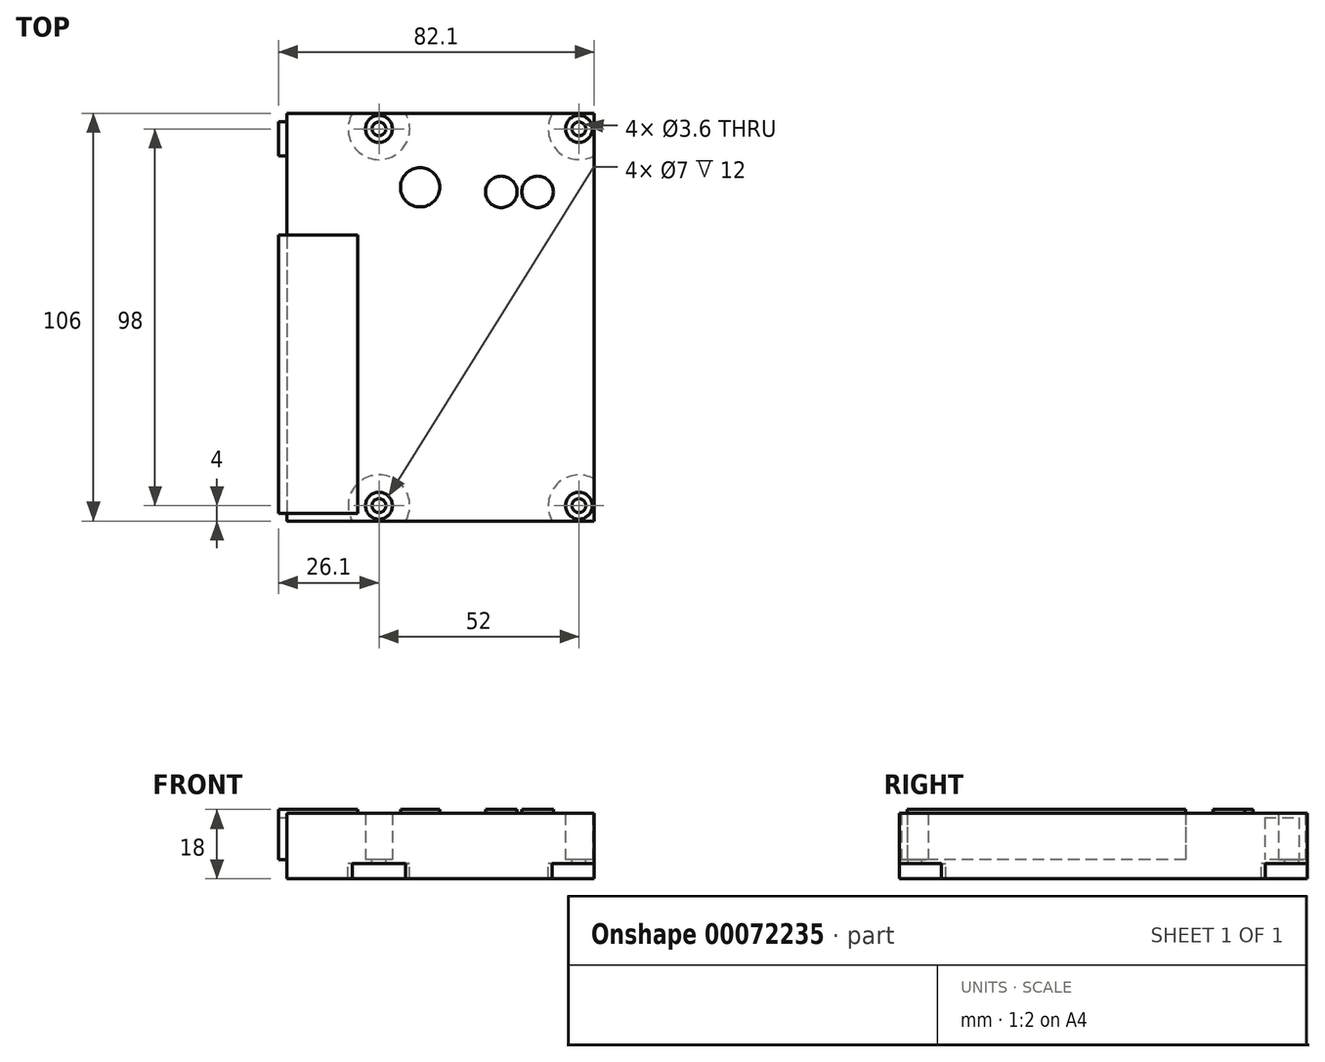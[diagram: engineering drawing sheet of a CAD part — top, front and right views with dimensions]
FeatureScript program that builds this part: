
annotation { "Feature Type Name" : "Feature", "Feature Type Description" : "" }
export const myFeature = defineFeature(function(context is Context, id is Id, definition is map)
    precondition{}
    {
        {
            var Q0;
            Q0=qCreatedBy(makeId("Top.planeOp"),FACE);
            var sketch = newSketch(context, id + "F0", { "sketchPlane" : qUnion([Q0])});
            skLineSegment(sketch, "E0.bottom", {"start": v(-40, 53) * mm, "end": v(40, 53) * mm});
            skLineSegment(sketch, "E0.top", {"start": v(-40, -53) * mm, "end": v(40, -53) * mm});
            skLineSegment(sketch, "E0.left", {"start": v(-40, 53) * mm, "end": v(-40, -53) * mm});
            skLineSegment(sketch, "E0.right", {"start": v(40, 53) * mm, "end": v(40, -53) * mm});
            skCircle(sketch, "E1", {"center": v(-16, 49) * mm, "radius": 1.8 * mm});
            skCircle(sketch, "E2", {"center": v(36, 49) * mm, "radius": 1.8 * mm});
            skCircle(sketch, "E3", {"center": v(-16, -49) * mm, "radius": 1.8 * mm});
            skCircle(sketch, "E4", {"center": v(36, -49) * mm, "radius": 1.8 * mm});
            skSolve(sketch);
        }
        {
            var Q0;
            Q0=qSketchRegion(id+"F0",true);
            extrude(context, id + "F1", {"entities" : qUnion([Q0]), "oppositeDirection" : true, "depth" : 1 * mm});
        }
        {
            var Q0;
            Q0=makeQuery(id+"F1.opExtrude","CAP_FACE",FACE,{"disambiguationData":[OSD([sQuery(id+"F0.wireOp",EDGE,"E0.bottom"),sQuery(id+"F0.wireOp",EDGE,"E0.top"),sQuery(id+"F0.wireOp",EDGE,"E0.left"),sQuery(id+"F0.wireOp",EDGE,"E0.right"),sQuery(id+"F0.wireOp",EDGE,"E1"),sQuery(id+"F0.wireOp",EDGE,"E2"),sQuery(id+"F0.wireOp",EDGE,"E3"),sQuery(id+"F0.wireOp",EDGE,"E4")])],"isStart":true});
            var sketch = newSketch(context, id + "F2", { "sketchPlane" : qUnion([Q0])});
            skLineSegment(sketch, "E5.bottom", {"start": v(-42.1, 21.4) * mm, "end": v(-21.5, 21.4) * mm});
            skLineSegment(sketch, "E5.top", {"start": v(-42.1, -51) * mm, "end": v(-21.5, -51) * mm});
            skLineSegment(sketch, "E5.left", {"start": v(-42.1, 21.4) * mm, "end": v(-42.1, -51) * mm});
            skLineSegment(sketch, "E5.right", {"start": v(-21.5, 21.4) * mm, "end": v(-21.5, -51) * mm});
            skSolve(sketch);
        }
        {
            var Q0;
            Q0=qSketchRegion(id+"F2",true);
            extrude(context, id + "F3", {"entities" : qUnion([Q0]), "operationType" : NewBodyOperationType.ADD, "depth" : 13 * mm});
        }
        {
            var Q0;
            Q0=makeQuery(id+"F1.opExtrude","CAP_FACE",FACE,{"disambiguationData":[OSD([sQuery(id+"F0.wireOp",EDGE,"E0.bottom"),sQuery(id+"F0.wireOp",EDGE,"E0.top"),sQuery(id+"F0.wireOp",EDGE,"E0.left"),sQuery(id+"F0.wireOp",EDGE,"E0.right"),sQuery(id+"F0.wireOp",EDGE,"E1"),sQuery(id+"F0.wireOp",EDGE,"E2"),sQuery(id+"F0.wireOp",EDGE,"E3"),sQuery(id+"F0.wireOp",EDGE,"E4")])],"isStart":true});
            var sketch = newSketch(context, id + "F4", { "sketchPlane" : qUnion([Q0])});
            skLineSegment(sketch, "E6.bottom", {"start": v(-42.1, 50.8) * mm, "end": v(-32.1, 50.8) * mm});
            skLineSegment(sketch, "E6.top", {"start": v(-42.1, 41.9) * mm, "end": v(-32.1, 41.9) * mm});
            skLineSegment(sketch, "E6.left", {"start": v(-42.1, 50.8) * mm, "end": v(-42.1, 41.9) * mm});
            skLineSegment(sketch, "E6.right", {"start": v(-32.1, 50.8) * mm, "end": v(-32.1, 41.9) * mm});
            skSolve(sketch);
        }
        {
            var Q0;
            Q0=qSketchRegion(id+"F4",true);
            extrude(context, id + "F5", {"entities" : qUnion([Q0]), "operationType" : NewBodyOperationType.ADD, "depth" : 10.9 * mm});
        }
        {
            var Q0;
            Q0=makeQuery(id+"F1.opExtrude","CAP_FACE",FACE,{"disambiguationData":[OSD([sQuery(id+"F0.wireOp",EDGE,"E0.bottom"),sQuery(id+"F0.wireOp",EDGE,"E0.top"),sQuery(id+"F0.wireOp",EDGE,"E0.left"),sQuery(id+"F0.wireOp",EDGE,"E0.right"),sQuery(id+"F0.wireOp",EDGE,"E1"),sQuery(id+"F0.wireOp",EDGE,"E2"),sQuery(id+"F0.wireOp",EDGE,"E3"),sQuery(id+"F0.wireOp",EDGE,"E4")])],"isStart":true});
            var sketch = newSketch(context, id + "F6", { "sketchPlane" : qUnion([Q0])});
            skCircle(sketch, "E7", {"center": v(-5.3, 33.8) * mm, "radius": 5.1 * mm});
            skCircle(sketch, "E8", {"center": v(15.8, 32.6) * mm, "radius": 4.1 * mm});
            skCircle(sketch, "E9", {"center": v(25.24, 32.6) * mm, "radius": 4.1 * mm});
            skSolve(sketch);
        }
        {
            var Q0;
            Q0=makeQuery(id+"F6.imprint","IMPRINT",FACE,{"disambiguationData":[TD([[makeQuery(id+"F6.imprint","IMPRINT",EDGE,{"derivedFrom":sQuery(id+"F6.wireOp",EDGE,"E7")}),1.0]])]});
            var Q1;
            Q1=makeQuery(id+"F6.imprint","IMPRINT",FACE,{"disambiguationData":[TD([[makeQuery(id+"F6.imprint","IMPRINT",EDGE,{"derivedFrom":sQuery(id+"F6.wireOp",EDGE,"E8")}),1.0]])]});
            var Q2;
            Q2=makeQuery(id+"F6.imprint","IMPRINT",FACE,{"disambiguationData":[TD([[makeQuery(id+"F6.imprint","IMPRINT",EDGE,{"derivedFrom":sQuery(id+"F6.wireOp",EDGE,"E9")}),1.0]])]});
            extrude(context, id + "F7", {"entities" : qUnion([Q0, Q1, Q2]), "operationType" : NewBodyOperationType.ADD, "depth" : 13 * mm});
        }
        {
            var Q0;
            Q0=makeQuery(id+"F1.opExtrude","CAP_FACE",FACE,{"disambiguationData":[OSD([sQuery(id+"F0.wireOp",EDGE,"E0.bottom"),sQuery(id+"F0.wireOp",EDGE,"E0.top"),sQuery(id+"F0.wireOp",EDGE,"E0.left"),sQuery(id+"F0.wireOp",EDGE,"E0.right"),sQuery(id+"F0.wireOp",EDGE,"E1"),sQuery(id+"F0.wireOp",EDGE,"E2"),sQuery(id+"F0.wireOp",EDGE,"E3"),sQuery(id+"F0.wireOp",EDGE,"E4")])],"isStart":false});
            var sketch = newSketch(context, id + "F8", { "sketchPlane" : qUnion([Q0])});
            skLineSegment(sketch, "E10.0", {"start": v(-40, 53) * mm, "end": v(40, 53) * mm});
            skLineSegment(sketch, "E11.0", {"start": v(40, -53) * mm, "end": v(40, 53) * mm});
            skLineSegment(sketch, "E12.0", {"start": v(-40, -53) * mm, "end": v(40, -53) * mm});
            skLineSegment(sketch, "E13.0", {"start": v(-40, -53) * mm, "end": v(-40, 53) * mm});
            skArc(sketch, "E14", {"start": v(-22.93, 53) * mm, "mid": v(-16, 41) * mm, "end": v(-9.07, 53) * mm});
            skArc(sketch, "E15", {"start": v(29.07, 53) * mm, "mid": v(30.34, 43.34) * mm, "end": v(40, 42.07) * mm});
            skArc(sketch, "E16", {"start": v(40, -42.07) * mm, "mid": v(30.34, -43.34) * mm, "end": v(29.07, -53) * mm});
            skArc(sketch, "E17", {"start": v(-9.07, -53) * mm, "mid": v(-16, -41) * mm, "end": v(-22.93, -53) * mm});
            skSolve(sketch);
        }
        {
            var Q0;
            {var subQ0=sQuery(id+"F8.wireOp",EDGE,"E13.0");Q0=makeQuery(id+"F8.imprint","IMPRINT",FACE,{"disambiguationData":[TD([[makeQuery(id+"F8.imprint","IMPRINT",EDGE,{"derivedFrom":subQ0}),-1.0]])]});}
            extrude(context, id + "F9", {"entities" : qUnion([Q0]), "operationType" : NewBodyOperationType.ADD, "depth" : 4 * mm});
        }
        {
            var Q0;
            Q0=makeQuery(id+"F1.opExtrude","CAP_FACE",FACE,{"disambiguationData":[OSD([sQuery(id+"F0.wireOp",EDGE,"E0.bottom"),sQuery(id+"F0.wireOp",EDGE,"E0.top"),sQuery(id+"F0.wireOp",EDGE,"E0.left"),sQuery(id+"F0.wireOp",EDGE,"E0.right"),sQuery(id+"F0.wireOp",EDGE,"E1"),sQuery(id+"F0.wireOp",EDGE,"E2"),sQuery(id+"F0.wireOp",EDGE,"E3"),sQuery(id+"F0.wireOp",EDGE,"E4")])],"isStart":true});
            var sketch = newSketch(context, id + "F10", { "sketchPlane" : qUnion([Q0])});
            skCircle(sketch, "E18", {"center": v(36, 49) * mm, "radius": 3.5 * mm});
            skCircle(sketch, "E19", {"center": v(-16, 49) * mm, "radius": 3.5 * mm});
            skCircle(sketch, "E20", {"center": v(-16, -49) * mm, "radius": 3.5 * mm});
            skCircle(sketch, "E21", {"center": v(36, -49) * mm, "radius": 3.5 * mm});
            skLineSegment(sketch, "E22.bottom", {"start": v(40, 53) * mm, "end": v(-40, 53) * mm});
            skLineSegment(sketch, "E22.top", {"start": v(40, -53) * mm, "end": v(-40, -53) * mm});
            skLineSegment(sketch, "E22.left", {"start": v(40, 53) * mm, "end": v(40, -53) * mm});
            skLineSegment(sketch, "E22.right", {"start": v(-40, 53) * mm, "end": v(-40, -53) * mm});
            skSolve(sketch);
        }
        {
            var Q0;
            Q0=qSketchRegion(id+"F10",true);
            extrude(context, id + "F11", {"entities" : qUnion([Q0]), "operationType" : NewBodyOperationType.ADD, "depth" : 12 * mm});
        }
    });
